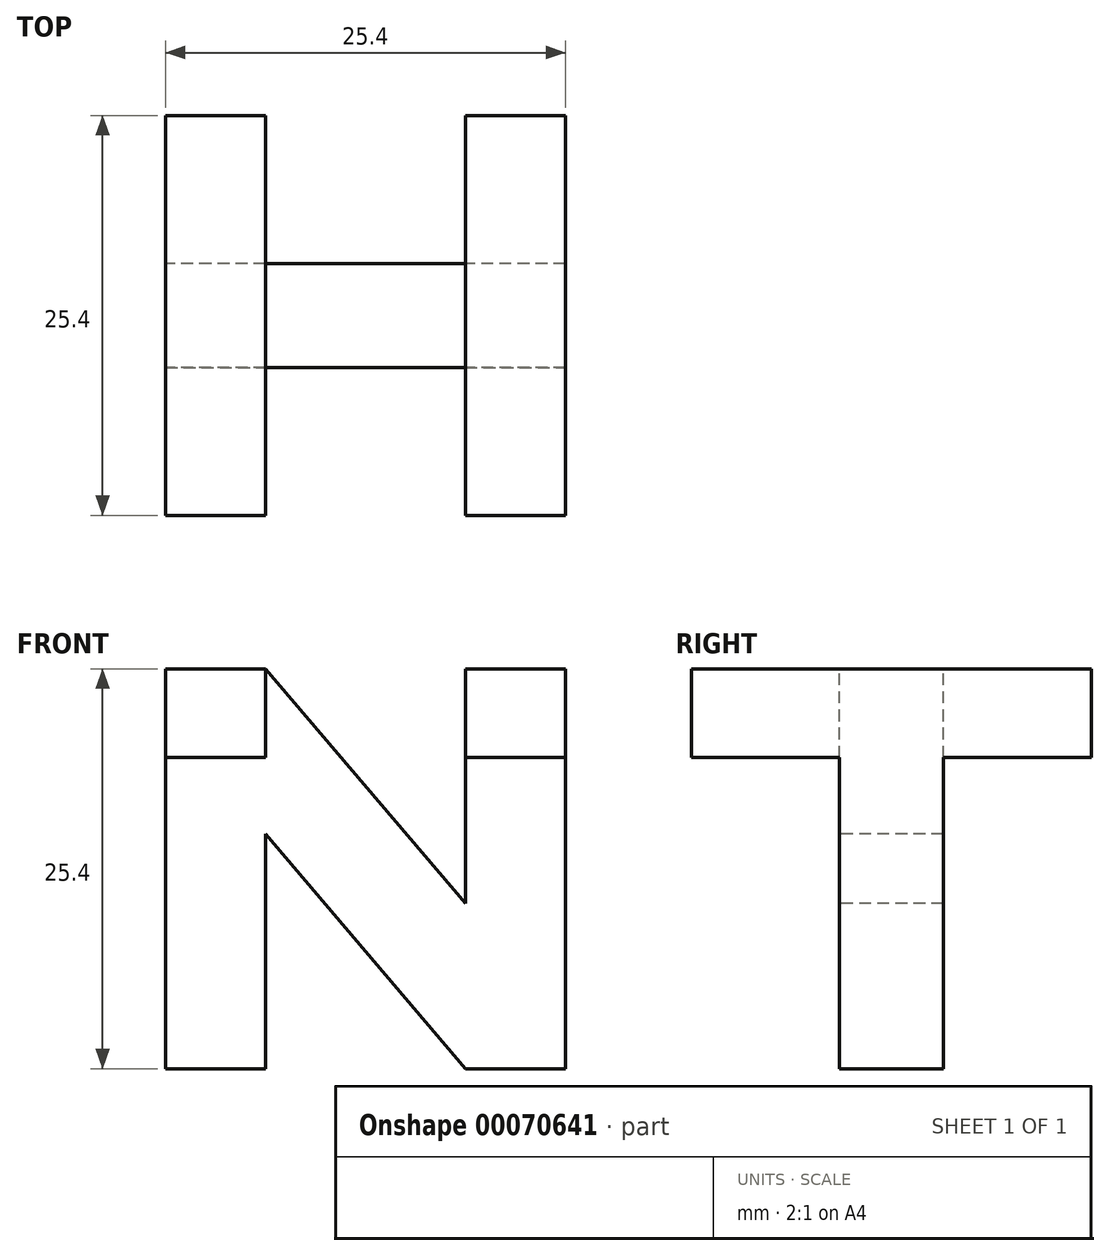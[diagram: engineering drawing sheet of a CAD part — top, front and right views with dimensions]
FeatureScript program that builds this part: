
annotation { "Feature Type Name" : "Feature", "Feature Type Description" : "" }
export const myFeature = defineFeature(function(context is Context, id is Id, definition is map)
    precondition{}
    {
        {
            var Q0;
            Q0=qCreatedBy(makeId("Top.planeOp"),FACE);
            var sketch = newSketch(context, id + "F0", { "sketchPlane" : qUnion([Q0])});
            skLineSegment(sketch, "E0.rect.bottom", {"start": v(12.7, 12.7) * mm, "end": v(-12.7, 12.7) * mm});
            skLineSegment(sketch, "E0.rect.top", {"start": v(12.7, -12.7) * mm, "end": v(-12.7, -12.7) * mm});
            skLineSegment(sketch, "E0.rect.left", {"start": v(12.7, 12.7) * mm, "end": v(12.7, -12.7) * mm});
            skLineSegment(sketch, "E0.rect.right", {"start": v(-12.7, 12.7) * mm, "end": v(-12.7, -12.7) * mm});
            skPoint(sketch, "E0.rect.middle", {"position": v(0, 0) * mm});
            skSolve(sketch);
        }
        {
            var Q0;
            Q0=makeQuery(id+"F0.imprint","IMPRINT",FACE,{"disambiguationData":[TD([[makeQuery(id+"F0.imprint","IMPRINT",EDGE,{"derivedFrom":sQuery(id+"F0.wireOp",EDGE,"E0.rect.bottom")}),1.0]])]});
            extrude(context, id + "F1", {"entities" : qUnion([Q0]), "depth" : 25.4 * mm});
        }
        {
            var Q0;
            Q0=makeQuery(id+"F1.opExtrude","CAP_FACE",FACE,{"disambiguationData":[OSD([sQuery(id+"F0.wireOp",EDGE,"E0.rect.bottom"),sQuery(id+"F0.wireOp",EDGE,"E0.rect.top"),sQuery(id+"F0.wireOp",EDGE,"E0.rect.left"),sQuery(id+"F0.wireOp",EDGE,"E0.rect.right")])],"isStart":false});
            var sketch = newSketch(context, id + "F2", { "sketchPlane" : qUnion([Q0])});
            skLineSegment(sketch, "E1", {"start": v(-12.7, 12.7) * mm, "end": v(-12.7, -12.7) * mm});
            skLineSegment(sketch, "E2", {"start": v(-12.7, -12.7) * mm, "end": v(-6.36, -12.7) * mm});
            skLineSegment(sketch, "E3", {"start": v(-6.36, 12.7) * mm, "end": v(-12.7, 12.7) * mm});
            skLineSegment(sketch, "E4", {"start": v(0, 0) * mm, "end": v(0, 12.7) * mm, "construction": true});
            skLineSegment(sketch, "E5", {"start": v(0, 0) * mm, "end": v(-12.7, 0) * mm, "construction": true});
            skLineSegment(sketch, "E6", {"start": v(-6.36, 12.7) * mm, "end": v(-6.36, 3.3) * mm});
            skLineSegment(sketch, "E7", {"start": v(-6.36, 3.3) * mm, "end": v(0, 3.3) * mm});
            skLineSegment(sketch, "E8.MirrorCS", {"start": v(-6.36, -12.7) * mm, "end": v(-12.7, -12.7) * mm});
            skLineSegment(sketch, "E9.MirrorCS", {"start": v(-6.36, -3.3) * mm, "end": v(0, -3.3) * mm});
            skLineSegment(sketch, "E10.MirrorCS", {"start": v(-6.36, -12.7) * mm, "end": v(-6.36, -3.3) * mm});
            skLineSegment(sketch, "E11.MirrorCS", {"start": v(6.36, -12.7) * mm, "end": v(12.7, -12.7) * mm});
            skLineSegment(sketch, "E12.MirrorCS", {"start": v(6.36, -12.7) * mm, "end": v(6.36, -3.3) * mm});
            skLineSegment(sketch, "E13.MirrorCS", {"start": v(6.36, -3.3) * mm, "end": v(0, -3.3) * mm});
            skLineSegment(sketch, "E14.MirrorCS", {"start": v(12.7, 12.7) * mm, "end": v(12.7, -12.7) * mm});
            skLineSegment(sketch, "E15.MirrorCS", {"start": v(12.7, -12.7) * mm, "end": v(6.36, -12.7) * mm});
            skLineSegment(sketch, "E16.MirrorCS", {"start": v(6.36, 12.7) * mm, "end": v(12.7, 12.7) * mm});
            skLineSegment(sketch, "E17.MirrorCS", {"start": v(6.36, 3.3) * mm, "end": v(0, 3.3) * mm});
            skLineSegment(sketch, "E18.MirrorCS", {"start": v(6.36, 12.7) * mm, "end": v(6.36, 3.3) * mm});
            skSolve(sketch);
        }
        {
            var Q0;
            Q0=makeQuery(id+"F1.opExtrude","SWEPT_FACE",FACE,{"disambiguationData":[OSD([sQuery(id+"F0.wireOp",EDGE,"E0.rect.right")])]});
            var sketch = newSketch(context, id + "F3", { "sketchPlane" : qUnion([Q0])});
            skLineSegment(sketch, "E19", {"start": v(-12.7, 25.4) * mm, "end": v(-12.7, 19.76) * mm});
            skLineSegment(sketch, "E20", {"start": v(-12.7, 19.76) * mm, "end": v(-3.3, 19.76) * mm});
            skLineSegment(sketch, "E21", {"start": v(-3.3, 19.76) * mm, "end": v(-3.3, 0) * mm});
            skLineSegment(sketch, "E22", {"start": v(-3.3, 0) * mm, "end": v(0, 0) * mm});
            skLineSegment(sketch, "E23", {"start": v(0, 0) * mm, "end": v(0, 25.4) * mm, "construction": true});
            skLineSegment(sketch, "E24", {"start": v(0, 25.4) * mm, "end": v(-12.7, 25.4) * mm});
            skLineSegment(sketch, "E25.MirrorCS", {"start": v(0, 25.4) * mm, "end": v(12.7, 25.4) * mm});
            skLineSegment(sketch, "E26.MirrorCS", {"start": v(12.7, 25.4) * mm, "end": v(12.7, 19.76) * mm});
            skLineSegment(sketch, "E27.MirrorCS", {"start": v(12.7, 19.76) * mm, "end": v(3.3, 19.76) * mm});
            skLineSegment(sketch, "E28.MirrorCS", {"start": v(3.3, 19.76) * mm, "end": v(3.3, 0) * mm});
            skLineSegment(sketch, "E29.MirrorCS", {"start": v(3.3, 0) * mm, "end": v(0, 0) * mm});
            skSolve(sketch);
        }
        {
            var Q0;
            Q0=makeQuery(id+"F1.opExtrude","SWEPT_FACE",FACE,{"disambiguationData":[OSD([sQuery(id+"F0.wireOp",EDGE,"E0.rect.top")])]});
            var sketch = newSketch(context, id + "F4", { "sketchPlane" : qUnion([Q0])});
            skLineSegment(sketch, "E30", {"start": v(-12.7, 25.4) * mm, "end": v(-12.7, 0) * mm});
            skLineSegment(sketch, "E31", {"start": v(-12.7, 0) * mm, "end": v(-6.34, 0) * mm});
            skLineSegment(sketch, "E32", {"start": v(-6.34, 0) * mm, "end": v(-6.34, 14.9) * mm});
            skLineSegment(sketch, "E33", {"start": v(-6.34, 14.9) * mm, "end": v(6.34, 0) * mm});
            skLineSegment(sketch, "E34", {"start": v(6.34, 0) * mm, "end": v(12.7, 0) * mm});
            skLineSegment(sketch, "E35", {"start": v(-12.7, 0) * mm, "end": v(12.7, 25.4) * mm, "construction": true});
            skPoint(sketch, "E36", {"position": v(0, 12.7) * mm});
            skLineSegment(sketch, "E37.1.0", {"start": v(6.34, 25.4) * mm, "end": v(6.34, 10.5) * mm});
            skLineSegment(sketch, "E37.1.1", {"start": v(12.7, 25.4) * mm, "end": v(6.34, 25.4) * mm});
            skLineSegment(sketch, "E37.1.2", {"start": v(12.7, 0) * mm, "end": v(12.7, 25.4) * mm});
            skLineSegment(sketch, "E37.1.3", {"start": v(6.34, 10.5) * mm, "end": v(-6.34, 25.4) * mm});
            skLineSegment(sketch, "E37.1.4", {"start": v(-6.34, 25.4) * mm, "end": v(-12.7, 25.4) * mm});
            skSolve(sketch);
        }
        {
            var Q0;
            Q0=makeQuery(id+"F2.imprint","IMPRINT",FACE,{"disambiguationData":[TD([[makeQuery(id+"F2.imprint","IMPRINT",EDGE,{"derivedFrom":sQuery(id+"F2.wireOp",EDGE,"E1")}),1.0]])]});
            extrude(context, id + "F5", {"entities" : qUnion([Q0]), "operationType" : NewBodyOperationType.INTERSECT, "endBound" : BoundingType.THROUGH_ALL, "oppositeDirection" : true, "depth" : 25.4 * mm});
        }
        {
            var Q0;
            Q0=makeQuery(id+"F3.imprint","IMPRINT",FACE,{"disambiguationData":[TD([[makeQuery(id+"F3.imprint","IMPRINT",EDGE,{"derivedFrom":sQuery(id+"F3.wireOp",EDGE,"E19")}),1.0]])]});
            extrude(context, id + "F6", {"entities" : qUnion([Q0]), "operationType" : NewBodyOperationType.INTERSECT, "endBound" : BoundingType.THROUGH_ALL, "oppositeDirection" : true, "depth" : 25.4 * mm});
        }
        {
            var Q0;
            Q0=makeQuery(id+"F4.imprint","IMPRINT",FACE,{"disambiguationData":[TD([[makeQuery(id+"F4.imprint","IMPRINT",EDGE,{"derivedFrom":sQuery(id+"F4.wireOp",EDGE,"E30")}),1.0]])]});
            extrude(context, id + "F7", {"entities" : qUnion([Q0]), "operationType" : NewBodyOperationType.INTERSECT, "endBound" : BoundingType.THROUGH_ALL, "oppositeDirection" : true, "depth" : 25.4 * mm});
        }
    });
